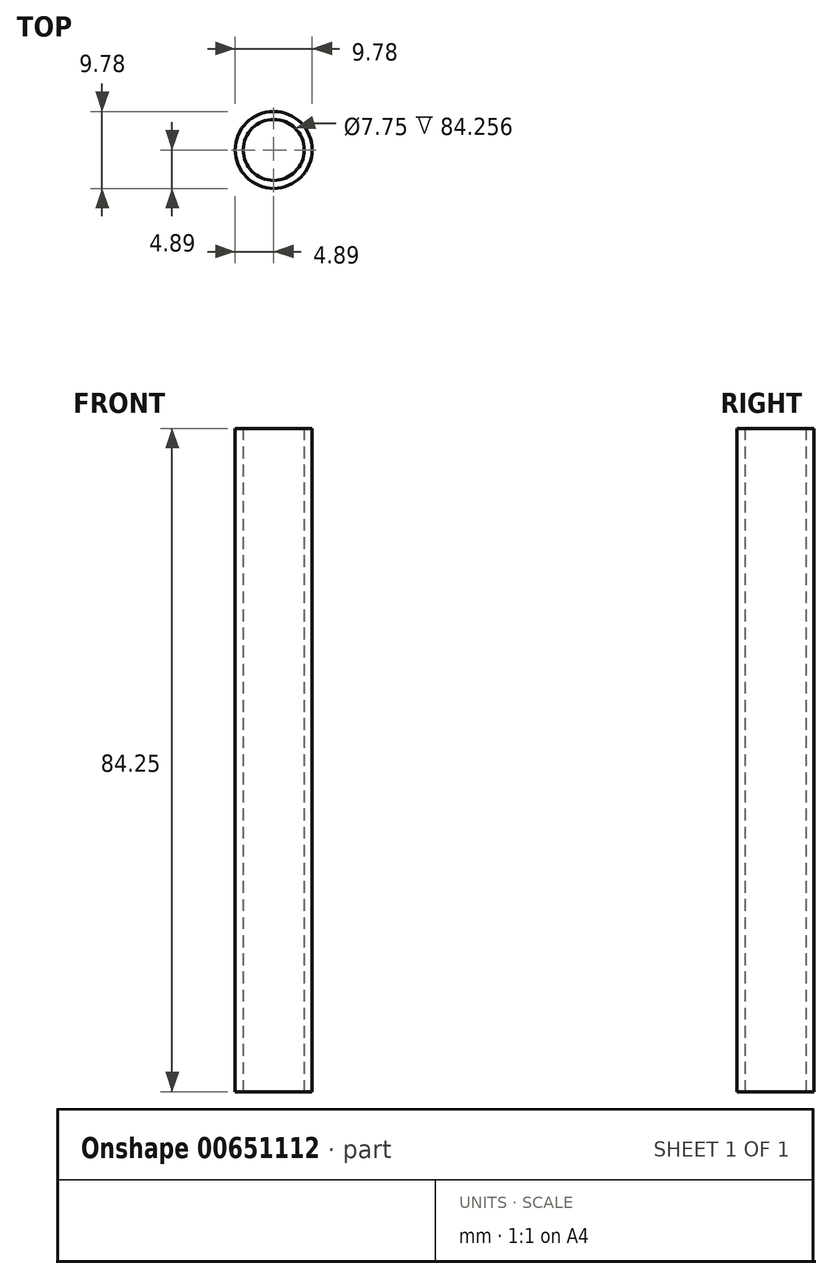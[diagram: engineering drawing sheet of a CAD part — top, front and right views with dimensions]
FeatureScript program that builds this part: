
annotation { "Feature Type Name" : "Feature", "Feature Type Description" : "" }
export const myFeature = defineFeature(function(context is Context, id is Id, definition is map)
    precondition{}
    {
        {
            var Q0;
            Q0=qCreatedBy(makeId("Right.planeOp"),FACE);
            var sketch = newSketch(context, id + "F0", { "sketchPlane" : qUnion([Q0])});
            skLineSegment(sketch, "E0", {"start": v(0, 23.44) * mm, "end": v(0, -60.81) * mm});
            skSolve(sketch);
        }
        {
            var Q0;
            Q0=sQuery(id+"F0.wireOp",EDGE,"E0");
            var Q1;
            Q1=sQuery(id+"F0.wireOp",VERTEX,"E0.start");
            cPlane(context, id + "F1", {"entities" : qUnion([Q0, Q1]), "cplaneType" : CPlaneType.LINE_POINT, "offset" : 25.4 * mm, "width" : 152.4 * mm, "height" : 152.4 * mm});
        }
        {
            var Q0;
            Q0=qCreatedBy(id+"F1.planeOp",FACE);
            var sketch = newSketch(context, id + "F2", { "sketchPlane" : qUnion([Q0])});
            skCircle(sketch, "E1", {"center": v(0, 0) * mm, "radius": 3.87 * mm});
            skCircle(sketch, "E2", {"center": v(0, 0) * mm, "radius": 4.89 * mm});
            skSolve(sketch);
        }
        {
            var Q0;
            Q0=makeQuery(id+"F2.imprint","IMPRINT",FACE,{"disambiguationData":[TD([[makeQuery(id+"F2.imprint","IMPRINT",EDGE,{"derivedFrom":sQuery(id+"F2.wireOp",EDGE,"E1")}),-1.0]])]});
            var Q1;
            Q1=sQuery(id+"F0.wireOp",EDGE,"E0");
            sweep(context, id + "F3", {"profiles" : qUnion([Q0]), "path" : qUnion([Q1])});
        }
    });
